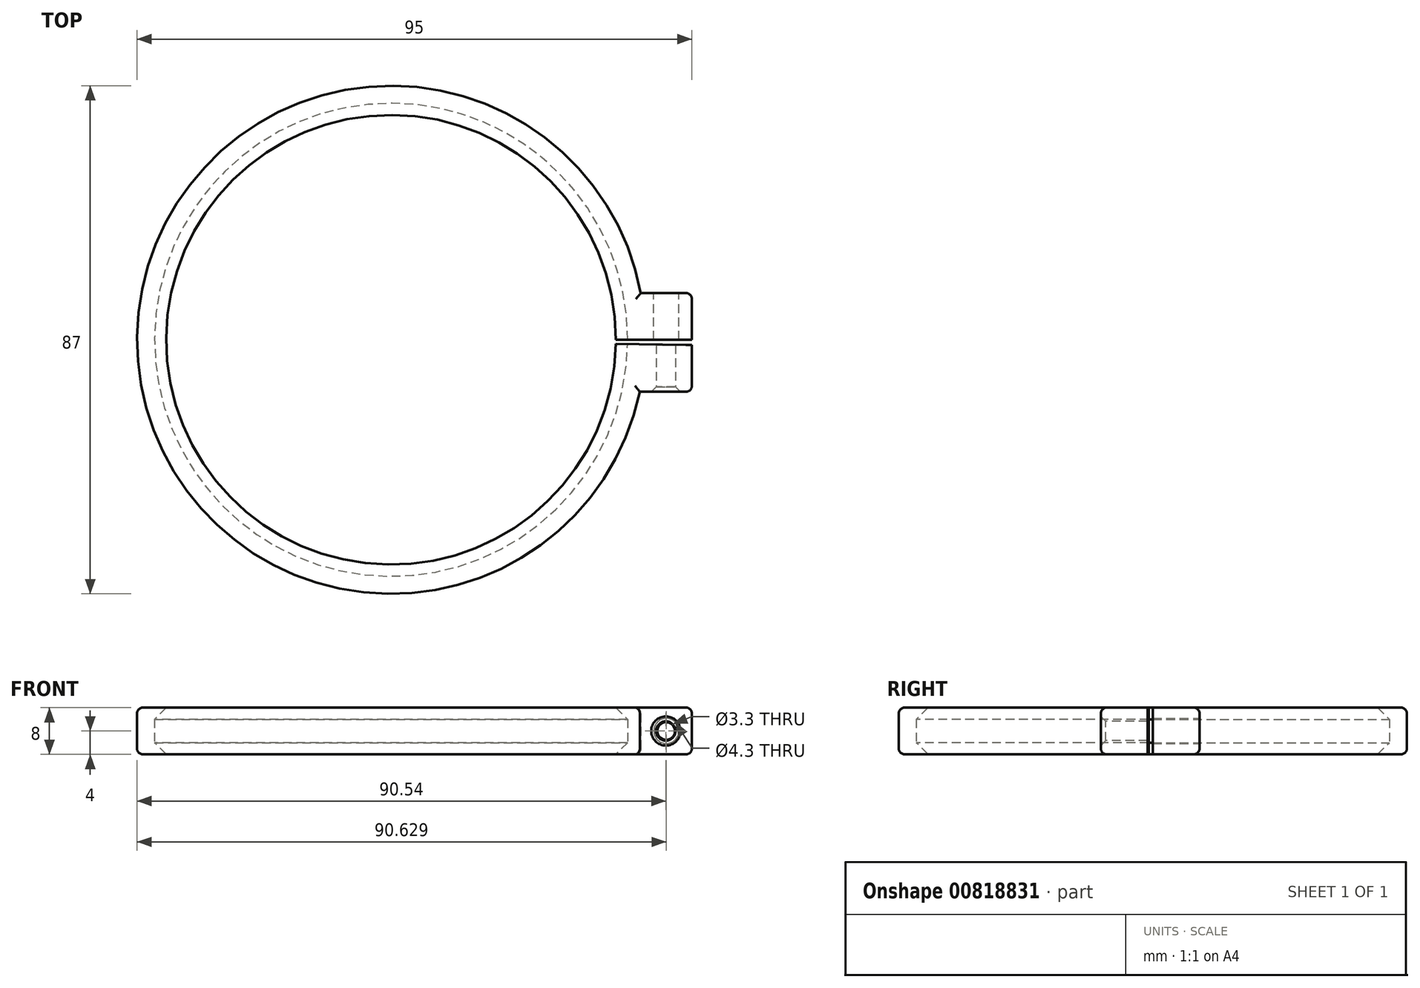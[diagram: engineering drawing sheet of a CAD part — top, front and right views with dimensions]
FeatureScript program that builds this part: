
annotation { "Feature Type Name" : "Feature", "Feature Type Description" : "" }
export const myFeature = defineFeature(function(context is Context, id is Id, definition is map)
    precondition{}
    {
        {
            var Q0;
            Q0=qCreatedBy(makeId("Front.planeOp"),FACE);
            var sketch = newSketch(context, id + "F0", { "sketchPlane" : qUnion([Q0])});
            skLineSegment(sketch, "E0", {"start": v(40.5, 2) * mm, "end": v(40.5, -2) * mm});
            skLineSegment(sketch, "E1", {"start": v(40.5, -2) * mm, "end": v(38.5, -4) * mm});
            skLineSegment(sketch, "E2", {"start": v(38.5, -4) * mm, "end": v(43.5, -4) * mm});
            skLineSegment(sketch, "E3", {"start": v(43.5, -4) * mm, "end": v(43.5, 4) * mm});
            skLineSegment(sketch, "E4", {"start": v(43.5, 4) * mm, "end": v(38.5, 4) * mm});
            skLineSegment(sketch, "E5", {"start": v(38.5, 4) * mm, "end": v(40.5, 2) * mm});
            skLineSegment(sketch, "E6", {"start": v(0, 0) * mm, "end": v(0, 27.72) * mm, "construction": true});
            skSolve(sketch);
        }
        {
            var Q0;
            Q0=makeQuery(id+"F0.imprint","IMPRINT",FACE,{"disambiguationData":[TD([[makeQuery(id+"F0.imprint","IMPRINT",EDGE,{"derivedFrom":sQuery(id+"F0.wireOp",EDGE,"E0")}),1.0]])]});
            var Q1;
            Q1=sQuery(id+"F0.wireOp",EDGE,"E6");
            revolve(context, id + "F1", {"surfaceOperationType" : NewSurfaceOperationType.NEW, "entities" : qUnion([Q0]), "axis" : qUnion([Q1]), "revolveType" : RevolveType.ONE_DIRECTION, "angle" : 359 * degree});
        }
        {
            var Q0;
            Q0=qCreatedBy(makeId("Top.planeOp"),FACE);
            var sketch = newSketch(context, id + "F2", { "sketchPlane" : qUnion([Q0])});
            skLineSegment(sketch, "E7.0", {"start": v(42.62, 0) * mm, "end": v(43.5, 0) * mm});
            skLineSegment(sketch, "E8.0", {"start": v(42.58, -0.74) * mm, "end": v(43.5, -0.76) * mm});
            skLineSegment(sketch, "E9", {"start": v(43.5, 0) * mm, "end": v(51.5, 0) * mm});
            skLineSegment(sketch, "E10", {"start": v(51.5, 8) * mm, "end": v(51.5, 0) * mm});
            skLineSegment(sketch, "E11", {"start": v(43.5, -0.76) * mm, "end": v(51.5, -0.9) * mm});
            skLineSegment(sketch, "E12", {"start": v(51.5, -0.9) * mm, "end": v(51.5, -8.9) * mm});
            skArc(sketch, "E13.0", {"start": v(42.58, -8.9) * mm, "mid": v(-43.5, 0.46) * mm, "end": v(42.76, 8) * mm});
            skLineSegment(sketch, "E14", {"start": v(51.5, 8) * mm, "end": v(42.76, 8) * mm});
            skLineSegment(sketch, "E15", {"start": v(42.76, 8) * mm, "end": v(42.62, 0) * mm});
            skLineSegment(sketch, "E16", {"start": v(51.5, -8.9) * mm, "end": v(42.58, -8.9) * mm});
            skLineSegment(sketch, "E17", {"start": v(42.58, -8.9) * mm, "end": v(42.58, -0.74) * mm});
            skPoint(sketch, "E18.orphan", {"position": v(43.5, 0) * mm});
            skPoint(sketch, "E19.orphan", {"position": v(43.5, -0.76) * mm});
            skPoint(sketch, "E20.orphan", {"position": v(38.5, -0.67) * mm});
            skPoint(sketch, "E21.orphan", {"position": v(38.5, 0) * mm});
            skSolve(sketch);
        }
        {
            var Q0;
            Q0=makeQuery(id+"F2.imprint","IMPRINT",FACE,{"disambiguationData":[TD([[makeQuery(id+"F2.imprint","IMPRINT",EDGE,{"derivedFrom":sQuery(id+"F2.wireOp",EDGE,"E9")}),1.0]])]});
            var Q1;
            Q1=makeQuery(id+"F2.imprint","IMPRINT",FACE,{"disambiguationData":[TD([[makeQuery(id+"F2.imprint","IMPRINT",EDGE,{"derivedFrom":sQuery(id+"F2.wireOp",EDGE,"E11")}),-1.0]])]});
            extrude(context, id + "F3", {"entities" : qUnion([Q0, Q1]), "operationType" : NewBodyOperationType.ADD, "endBound" : BoundingType.SYMMETRIC, "depth" : 8 * mm, "offsetDistance" : 25 * mm});
        }
        {
            var Q0;
            Q0=makeQuery(id+"F3.opExtrude","SWEPT_FACE",FACE,{"disambiguationData":[OSD([sQuery(id+"F2.wireOp",EDGE,"E16")])]});
            var sketch = newSketch(context, id + "F4", { "sketchPlane" : qUnion([Q0])});
            skPoint(sketch, "E22", {"position": v(47.04, 0) * mm});
            skPoint(sketch, "E22.positionSnap0", {"position": v(47.04, -4) * mm});
            skPoint(sketch, "E22.positionSnap1", {"position": v(51.5, 0) * mm});
            skSolve(sketch);
        }
        {
            var Q0;
            Q0=sQuery(id+"F4.wireOp",VERTEX,"E22");
            var Q1;
            Q1=makeQuery(id+"F1.opRevolve","SWEPT_BODY",BODY,{"disambiguationData":[OSD([sQuery(id+"F0.wireOp",EDGE,"E0"),sQuery(id+"F0.wireOp",EDGE,"E1"),sQuery(id+"F0.wireOp",EDGE,"E2"),sQuery(id+"F0.wireOp",EDGE,"E3"),sQuery(id+"F0.wireOp",EDGE,"E4"),sQuery(id+"F0.wireOp",EDGE,"E5")])]});
            hole(context, id + "F5", {"style" : HoleStyle.C_SINK, "endStyle" : HoleEndStyle.BLIND, "holeDiameter" : 3.3 * mm, "cSinkDiameter" : 5 * mm, "cSinkAngle" : 90 * degree, "majorDiameter" : 5 * mm, "holeDepth" : 8 * mm, "isTappedThrough" : true, "tappedDepth" : 100 * mm, "tapClearance" : 3, "startFromSketch" : true, "locations" : qUnion([Q0]), "scope" : qUnion([Q1])});
        }
        {
            var Q0;
            Q0=makeQuery(id+"F3.opExtrude","SWEPT_FACE",FACE,{"disambiguationData":[OSD([sQuery(id+"F2.wireOp",EDGE,"E14")])]});
            var sketch = newSketch(context, id + "F6", { "sketchPlane" : qUnion([Q0])});
            skPoint(sketch, "E23", {"position": v(-47.13, 0) * mm});
            skPoint(sketch, "E23.positionSnap0", {"position": v(-47.13, 4) * mm});
            skPoint(sketch, "E23.positionSnap1", {"position": v(-51.5, 0) * mm});
            skCircle(sketch, "E24", {"center": v(-47.13, 0) * mm, "radius": 2.15 * mm});
            skSolve(sketch);
        }
        {
            var Q0;
            Q0=makeQuery(id+"F6.imprint","IMPRINT",FACE,{"disambiguationData":[TD([[makeQuery(id+"F6.imprint","IMPRINT",EDGE,{"derivedFrom":sQuery(id+"F6.wireOp",EDGE,"E24")}),1.0]])]});
            var Q1;
            Q1=makeQuery(id+"F3.boolean.opBoolean","MERGE",FACE,{"derivedFrom":[makeQuery(id+"F1.opRevolve","CAP_FACE",FACE,{"disambiguationData":[OSD([sQuery(id+"F0.wireOp",EDGE,"E0"),sQuery(id+"F0.wireOp",EDGE,"E1"),sQuery(id+"F0.wireOp",EDGE,"E2"),sQuery(id+"F0.wireOp",EDGE,"E3"),sQuery(id+"F0.wireOp",EDGE,"E4"),sQuery(id+"F0.wireOp",EDGE,"E5")])],"isStart":true}),makeQuery(id+"F3.opExtrude","SWEPT_FACE",FACE,{"disambiguationData":[OSD([sQuery(id+"F2.wireOp",EDGE,"E9"),sQuery(id+"F2.wireOp",EDGE,"E7.0")])]})]});
            extrude(context, id + "F7", {"entities" : qUnion([Q0]), "operationType" : NewBodyOperationType.REMOVE, "endBound" : BoundingType.UP_TO_SURFACE, "oppositeDirection" : true, "depth" : 25 * mm, "endBoundEntityFace" : qUnion([Q1]), "offsetDistance" : 25 * mm});
        }
        {
            var Q0;
            Q0=makeQuery(id+"F3.opExtrude","CAP_EDGE",EDGE,{"disambiguationData":[OSD([sQuery(id+"F2.wireOp",EDGE,"E14")])],"isStart":true});
            var Q1;
            Q1=makeQuery(id+"F1.opRevolve","SWEPT_EDGE",EDGE,{"disambiguationData":[OSD([sQuery(id+"F0.wireOp",EDGE,"E2"),sQuery(id+"F0.wireOp",EDGE,"E3")])]});
            var Q2;
            Q2=makeQuery(id+"F3.opExtrude","CAP_EDGE",EDGE,{"disambiguationData":[OSD([sQuery(id+"F2.wireOp",EDGE,"E10")])],"isStart":true});
            var Q3;
            Q3=makeQuery(id+"F3.opExtrude","CAP_EDGE",EDGE,{"disambiguationData":[OSD([sQuery(id+"F2.wireOp",EDGE,"E12")])],"isStart":true});
            var Q4;
            Q4=makeQuery(id+"F3.opExtrude","CAP_EDGE",EDGE,{"disambiguationData":[OSD([sQuery(id+"F2.wireOp",EDGE,"E16")])],"isStart":true});
            var Q5;
            Q5=makeQuery(id+"F3.opExtrude","CAP_EDGE",EDGE,{"disambiguationData":[OSD([sQuery(id+"F2.wireOp",EDGE,"E10")])],"isStart":false});
            var Q6;
            Q6=makeQuery(id+"F3.opExtrude","CAP_EDGE",EDGE,{"disambiguationData":[OSD([sQuery(id+"F2.wireOp",EDGE,"E14")])],"isStart":false});
            var Q7;
            Q7=makeQuery(id+"F1.opRevolve","SWEPT_EDGE",EDGE,{"disambiguationData":[OSD([sQuery(id+"F0.wireOp",EDGE,"E3"),sQuery(id+"F0.wireOp",EDGE,"E4")])]});
            var Q8;
            Q8=makeQuery(id+"F3.opExtrude","CAP_EDGE",EDGE,{"disambiguationData":[OSD([sQuery(id+"F2.wireOp",EDGE,"E16")])],"isStart":false});
            var Q9;
            Q9=makeQuery(id+"F3.opExtrude","CAP_EDGE",EDGE,{"disambiguationData":[OSD([sQuery(id+"F2.wireOp",EDGE,"E12")])],"isStart":false});
            var Q10;
            Q10=makeQuery(id+"F3.opExtrude","SWEPT_EDGE",EDGE,{"disambiguationData":[OSD([sQuery(id+"F2.wireOp",EDGE,"E12"),sQuery(id+"F2.wireOp",EDGE,"E16")])]});
            var Q11;
            Q11=makeQuery(id+"F3.opExtrude","SWEPT_EDGE",EDGE,{"disambiguationData":[OSD([sQuery(id+"F2.wireOp",EDGE,"E10"),sQuery(id+"F2.wireOp",EDGE,"E14")])]});
            var Q12;
            Q12=makeQuery(id+"F3.opExtrude","SWEPT_EDGE",EDGE,{"disambiguationData":[OSD([sQuery(id+"F2.wireOp",EDGE,"E14"),sQuery(id+"F2.wireOp",EDGE,"E15")])]});
            var Q13;
            Q13=makeQuery(id+"F3.opExtrude","SWEPT_EDGE",EDGE,{"disambiguationData":[OSD([sQuery(id+"F2.wireOp",EDGE,"E16"),sQuery(id+"F2.wireOp",EDGE,"E17")])]});
            fillet(context, id + "F8", {"entities" : qUnion([Q0, Q1, Q2, Q3, Q4, Q5, Q6, Q7, Q8, Q9, Q10, Q11, Q12, Q13]), "radius" : 1 * mm, "tangentPropagation" : true, "allowEdgeOverflow" : false});
        }
    });
